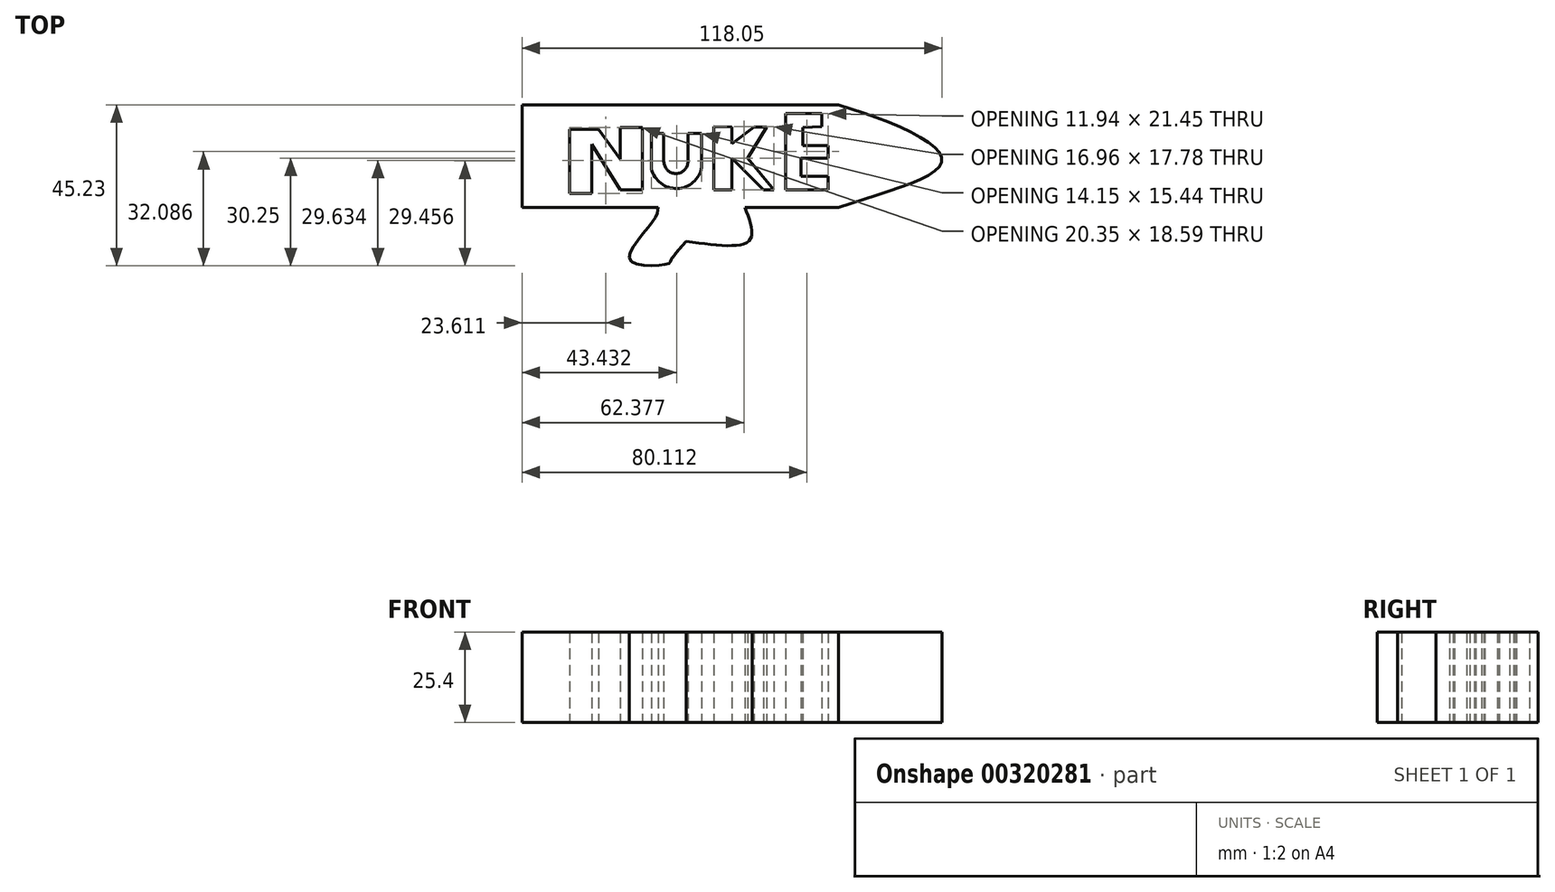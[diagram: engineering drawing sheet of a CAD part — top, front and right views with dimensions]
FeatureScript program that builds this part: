
annotation { "Feature Type Name" : "Feature", "Feature Type Description" : "" }
export const myFeature = defineFeature(function(context is Context, id is Id, definition is map)
    precondition{}
    {
        {
            var Q0;
            Q0=qCreatedBy(makeId("Top.planeOp"),FACE);
            var sketch = newSketch(context, id + "F0", { "sketchPlane" : qUnion([Q0])});
            skLineSegment(sketch, "E0.bottom", {"start": v(-27.6, 23.87) * mm, "end": v(61.3, 23.87) * mm});
            skLineSegment(sketch, "E0.top", {"start": v(-27.6, -4.92) * mm, "end": v(61.3, -4.92) * mm});
            skLineSegment(sketch, "E0.left", {"start": v(-27.6, 23.87) * mm, "end": v(-27.6, -4.92) * mm});
            skLineSegment(sketch, "E0.right", {"start": v(61.3, 23.87) * mm, "end": v(61.3, -4.92) * mm});
            skFitSpline(sketch, "E1", {"points": [v(61.3, 23.87) * mm, v(90.45, 8.33) * mm, v(61.3, -4.92) * mm], "startDerivative": vector(81.94, -23.98) * mm, "endDerivative": vector(-81.74, -26.81) * mm});
            skLineSegment(sketch, "E2", {"start": v(-14.15, 16.99) * mm, "end": v(-14.15, -1.02) * mm});
            skLineSegment(sketch, "E3", {"start": v(-14.15, -1.02) * mm, "end": v(-7.96, -1.02) * mm});
            skLineSegment(sketch, "E4", {"start": v(-7.96, -1.02) * mm, "end": v(-7.96, 12.78) * mm});
            skLineSegment(sketch, "E5", {"start": v(-7.96, 12.78) * mm, "end": v(0, 0) * mm});
            skLineSegment(sketch, "E6", {"start": v(0, 0) * mm, "end": v(6.2, 0) * mm});
            skLineSegment(sketch, "E7", {"start": v(6.2, 0) * mm, "end": v(6.2, 17.57) * mm});
            skLineSegment(sketch, "E8", {"start": v(6.2, 17.57) * mm, "end": v(0, 17.57) * mm});
            skLineSegment(sketch, "E9", {"start": v(0, 17.57) * mm, "end": v(0, 8.57) * mm});
            skLineSegment(sketch, "E10", {"start": v(0, 8.57) * mm, "end": v(-6.43, 17.45) * mm});
            skLineSegment(sketch, "E11", {"start": v(-14.15, 16.99) * mm, "end": v(-5.27, 16.99) * mm});
            skLineSegment(sketch, "E12", {"start": v(8.77, 15.82) * mm, "end": v(8.77, 5.88) * mm});
            skArc(sketch, "E13", {"start": v(8.77, 5.88) * mm, "mid": v(16.03, 0.38) * mm, "end": v(22.92, 6.34) * mm});
            skLineSegment(sketch, "E14", {"start": v(22.92, 6.34) * mm, "end": v(22.92, 15.82) * mm});
            skLineSegment(sketch, "E15", {"start": v(22.92, 15.82) * mm, "end": v(19.06, 15.82) * mm});
            skLineSegment(sketch, "E16", {"start": v(19.06, 15.82) * mm, "end": v(19.06, 7.98) * mm});
            skArc(sketch, "E17", {"start": v(12.28, 7.98) * mm, "mid": v(15.67, 4.59) * mm, "end": v(19.06, 7.98) * mm});
            skLineSegment(sketch, "E18", {"start": v(8.77, 15.82) * mm, "end": v(12.16, 15.82) * mm});
            skLineSegment(sketch, "E19", {"start": v(12.16, 15.82) * mm, "end": v(12.28, 7.98) * mm});
            skLineSegment(sketch, "E20", {"start": v(26.3, 17.78) * mm, "end": v(26.3, 0) * mm});
            skLineSegment(sketch, "E21", {"start": v(26.3, 0) * mm, "end": v(31.39, 0) * mm});
            skLineSegment(sketch, "E22", {"start": v(31.39, 0) * mm, "end": v(31.39, 8.9) * mm});
            skLineSegment(sketch, "E23", {"start": v(31.39, 8.9) * mm, "end": v(40.34, 0) * mm});
            skLineSegment(sketch, "E24", {"start": v(40.34, 0) * mm, "end": v(43.26, 0) * mm});
            skLineSegment(sketch, "E25", {"start": v(43.26, 0) * mm, "end": v(35.78, 8.89) * mm});
            skLineSegment(sketch, "E26", {"start": v(31.39, 17.69) * mm, "end": v(26.3, 17.78) * mm});
            skLineSegment(sketch, "E27", {"start": v(46.55, 17.78) * mm, "end": v(46.55, 0) * mm});
            skLineSegment(sketch, "E28", {"start": v(46.55, 0) * mm, "end": v(58.5, 0) * mm});
            skLineSegment(sketch, "E29", {"start": v(58.5, 0) * mm, "end": v(58.5, 3.81) * mm});
            skLineSegment(sketch, "E30", {"start": v(58.5, 3.81) * mm, "end": v(50.87, 3.81) * mm});
            skLineSegment(sketch, "E31", {"start": v(50.87, 3.8) * mm, "end": v(50.87, 8.89) * mm});
            skLineSegment(sketch, "E32", {"start": v(50.87, 8.9) * mm, "end": v(58.5, 8.9) * mm});
            skPoint(sketch, "E33.start.orphan", {"position": v(31.39, 21.59) * mm});
            skLineSegment(sketch, "E34", {"start": v(31.39, 17.69) * mm, "end": v(31.39, 12.89) * mm});
            skLineSegment(sketch, "E35", {"start": v(31.39, 12.89) * mm, "end": v(37.65, 17.69) * mm});
            skLineSegment(sketch, "E36", {"start": v(37.65, 17.69) * mm, "end": v(41.15, 17.62) * mm});
            skLineSegment(sketch, "E37", {"start": v(41.15, 17.62) * mm, "end": v(35.78, 8.89) * mm});
            skLineSegment(sketch, "E38", {"start": v(58.5, 8.89) * mm, "end": v(58.5, 12.42) * mm});
            skLineSegment(sketch, "E39", {"start": v(58.5, 12.42) * mm, "end": v(51.33, 12.42) * mm});
            skLineSegment(sketch, "E40", {"start": v(51.33, 12.42) * mm, "end": v(51.33, 17.5) * mm});
            skLineSegment(sketch, "E41", {"start": v(46.55, 17.78) * mm, "end": v(46.55, 21.45) * mm});
            skLineSegment(sketch, "E42", {"start": v(46.55, 21.45) * mm, "end": v(56.71, 21.45) * mm});
            skLineSegment(sketch, "E43", {"start": v(56.71, 21.45) * mm, "end": v(56.71, 17.78) * mm});
            skLineSegment(sketch, "E44", {"start": v(51.33, 17.5) * mm, "end": v(56.71, 17.78) * mm});
            skFitSpline(sketch, "E45", {"points": [v(10.7, -4.92) * mm, v(9.28, -8.77) * mm, v(2.82, -19.76) * mm, v(13.56, -20.77) * mm, v(14.4, -19.6) * mm, v(21.28, -10.78) * mm, v(22.7, -4.92) * mm], "startDerivative": vector(-2.13, -24.28) * mm, "endDerivative": vector(0.9, 34.72) * mm});
            skFitSpline(sketch, "E46", {"points": [v(35.06, -4.92) * mm, v(36.37, -14.19) * mm, v(18.55, -14.47) * mm], "startDerivative": vector(10.25, -26.58) * mm, "endDerivative": vector(-40.57, 5.77) * mm});
            skFitSpline(sketch, "E47", {"points": [v(27.98, -4.92) * mm, v(34.18, -9.95) * mm, v(21.28, -10.78) * mm], "startDerivative": vector(18.82, -13.1) * mm, "endDerivative": vector(-30.1, 0.77) * mm});
            skSolve(sketch);
        }
        {
            var Q0;
            Q0=makeQuery(id+"F0.imprint","IMPRINT",FACE,{"disambiguationData":[TD([[makeQuery(id+"F0.imprint","IMPRINT",EDGE,{"derivedFrom":sQuery(id+"F0.wireOp",EDGE,"E0.bottom")}),-1.0]])]});
            var Q1;
            {var subQ0=sQuery(id+"F0.wireOp",EDGE,"E45");var subQ1=sQuery(id+"F0.wireOp",EDGE,"E0.top");var subQ2=makeQuery(id+"F0.imprint","INTERSECT",VERTEX,{"disambiguationData":[OD(0.0)],"derivedFrom":[subQ1,subQ0]});Q1=makeQuery(id+"F0.imprint","IMPRINT",FACE,{"disambiguationData":[TD([[makeQuery(id+"F0.imprint","IMPRINT",EDGE,{"disambiguationData":[TD([[subQ2,-1.0]])],"derivedFrom":subQ1}),-1.0]])]});}
            var Q2;
            {var subQ0=sQuery(id+"F0.wireOp",EDGE,"E46");Q2=makeQuery(id+"F0.imprint","IMPRINT",FACE,{"disambiguationData":[TD([[makeQuery(id+"F0.imprint","IMPRINT",EDGE,{"derivedFrom":subQ0}),-1.0]])]});}
            var Q3;
            {var subQ3=sQuery(id+"F0.wireOp",EDGE,"E47");Q3=makeQuery(id+"F0.imprint","IMPRINT",FACE,{"disambiguationData":[TD([[makeQuery(id+"F0.imprint","IMPRINT",EDGE,{"derivedFrom":subQ3}),-1.0]])]});}
            var Q4;
            Q4=makeQuery(id+"F0.imprint","IMPRINT",FACE,{"disambiguationData":[TD([[makeQuery(id+"F0.imprint","IMPRINT",EDGE,{"derivedFrom":sQuery(id+"F0.wireOp",EDGE,"E0.right")}),1.0]])]});
            extrude(context, id + "F1", {"entities" : qUnion([Q0, Q1, Q2, Q3, Q4]), "depth" : 25.4 * mm});
        }
    });
